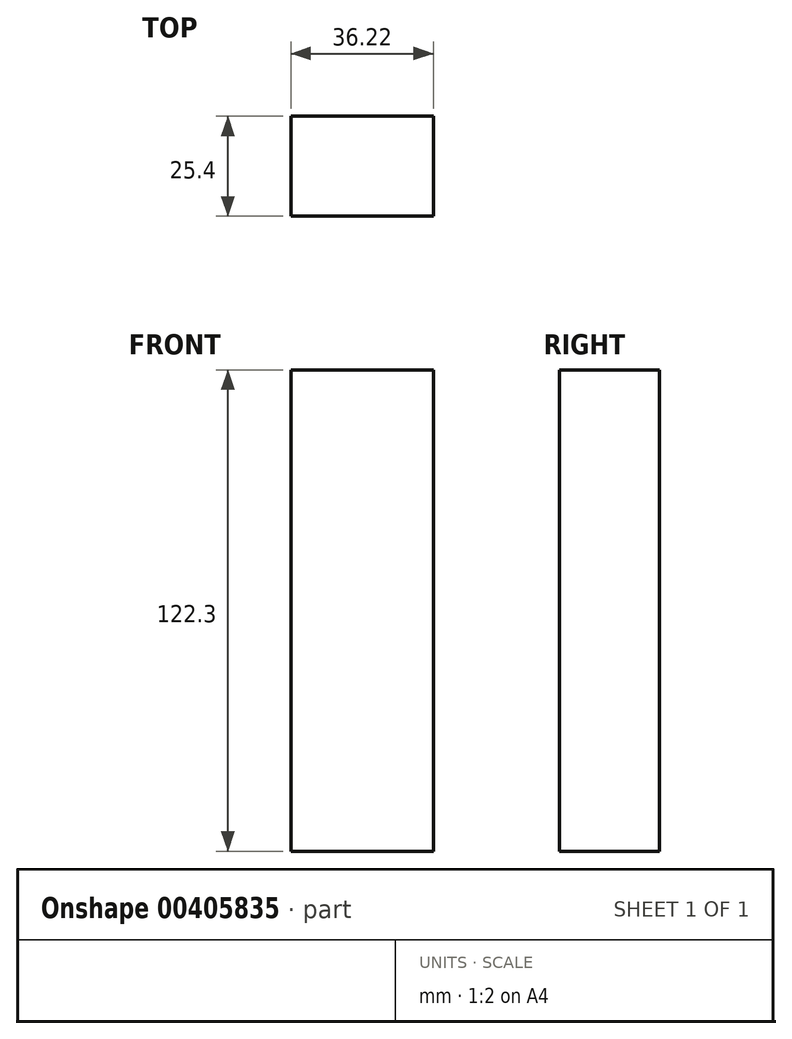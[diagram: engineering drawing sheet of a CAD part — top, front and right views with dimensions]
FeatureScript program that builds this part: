
annotation { "Feature Type Name" : "Feature", "Feature Type Description" : "" }
export const myFeature = defineFeature(function(context is Context, id is Id, definition is map)
    precondition{}
    {
        {
            var Q0;
            Q0=qCreatedBy(makeId("Front.planeOp"),FACE);
            var sketch = newSketch(context, id + "F0", { "sketchPlane" : qUnion([Q0])});
            skLineSegment(sketch, "E0.bottom", {"start": v(-18.11, -61.15) * mm, "end": v(18.11, -61.15) * mm});
            skLineSegment(sketch, "E0.top", {"start": v(-18.11, 61.15) * mm, "end": v(18.11, 61.15) * mm});
            skLineSegment(sketch, "E0.left", {"start": v(-18.11, -61.15) * mm, "end": v(-18.11, 61.15) * mm});
            skLineSegment(sketch, "E0.right", {"start": v(18.11, -61.15) * mm, "end": v(18.11, 61.15) * mm});
            skPoint(sketch, "E0.middle", {"position": v(0, 0) * mm});
            skSolve(sketch);
        }
        {
            var Q0;
            Q0=makeQuery(id+"F0.imprint","IMPRINT",FACE,{"disambiguationData":[TD([[makeQuery(id+"F0.imprint","IMPRINT",EDGE,{"derivedFrom":sQuery(id+"F0.wireOp",EDGE,"E0.bottom")}),1.0]])]});
            extrude(context, id + "F1", {"entities" : qUnion([Q0]), "endBound" : BoundingType.SYMMETRIC, "depth" : 25.4 * mm});
        }
    });
